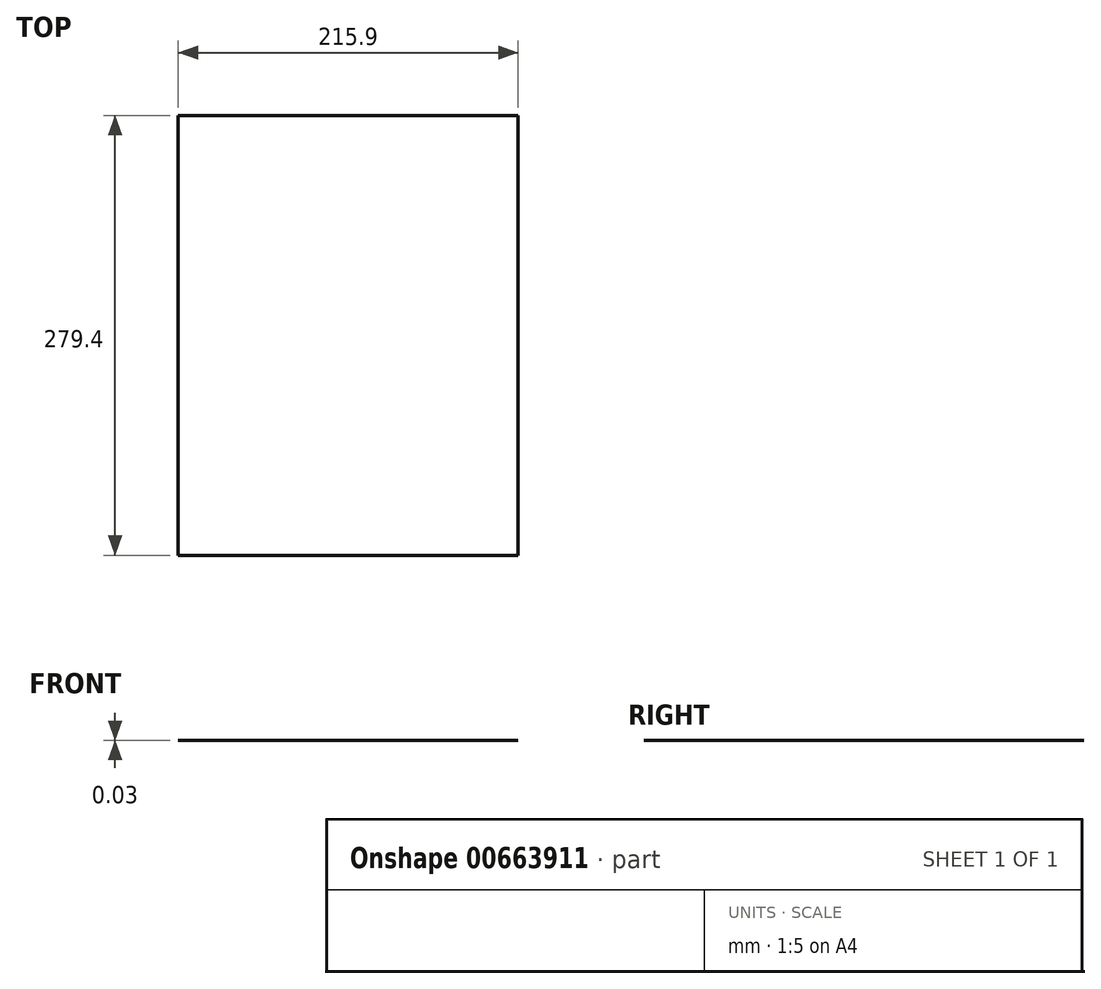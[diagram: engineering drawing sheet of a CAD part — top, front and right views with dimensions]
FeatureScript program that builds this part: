
annotation { "Feature Type Name" : "Feature", "Feature Type Description" : "" }
export const myFeature = defineFeature(function(context is Context, id is Id, definition is map)
    precondition{}
    {
        {
            var Q0;
            Q0=qCreatedBy(makeId("Top.planeOp"),FACE);
            var sketch = newSketch(context, id + "F0", { "sketchPlane" : qUnion([Q0])});
            skLineSegment(sketch, "E0", {"start": v(-118.73, 123.28) * mm, "end": v(-118.73, -156.12) * mm});
            skLineSegment(sketch, "E1", {"start": v(-118.73, -156.12) * mm, "end": v(97.17, -156.12) * mm});
            skLineSegment(sketch, "E2", {"start": v(97.17, -156.12) * mm, "end": v(97.17, 123.28) * mm});
            skLineSegment(sketch, "E3", {"start": v(97.17, 123.28) * mm, "end": v(-118.73, 123.28) * mm});
            skSolve(sketch);
        }
        {
            var Q0;
            Q0 = qSketchRegion(id + "F0", true);
            extrude(context, id + "F1", {"entities" : qUnion([Q0]), "depth" : 0.03 * mm, "offsetDistance" : 25.4 * mm});
        }
    });
